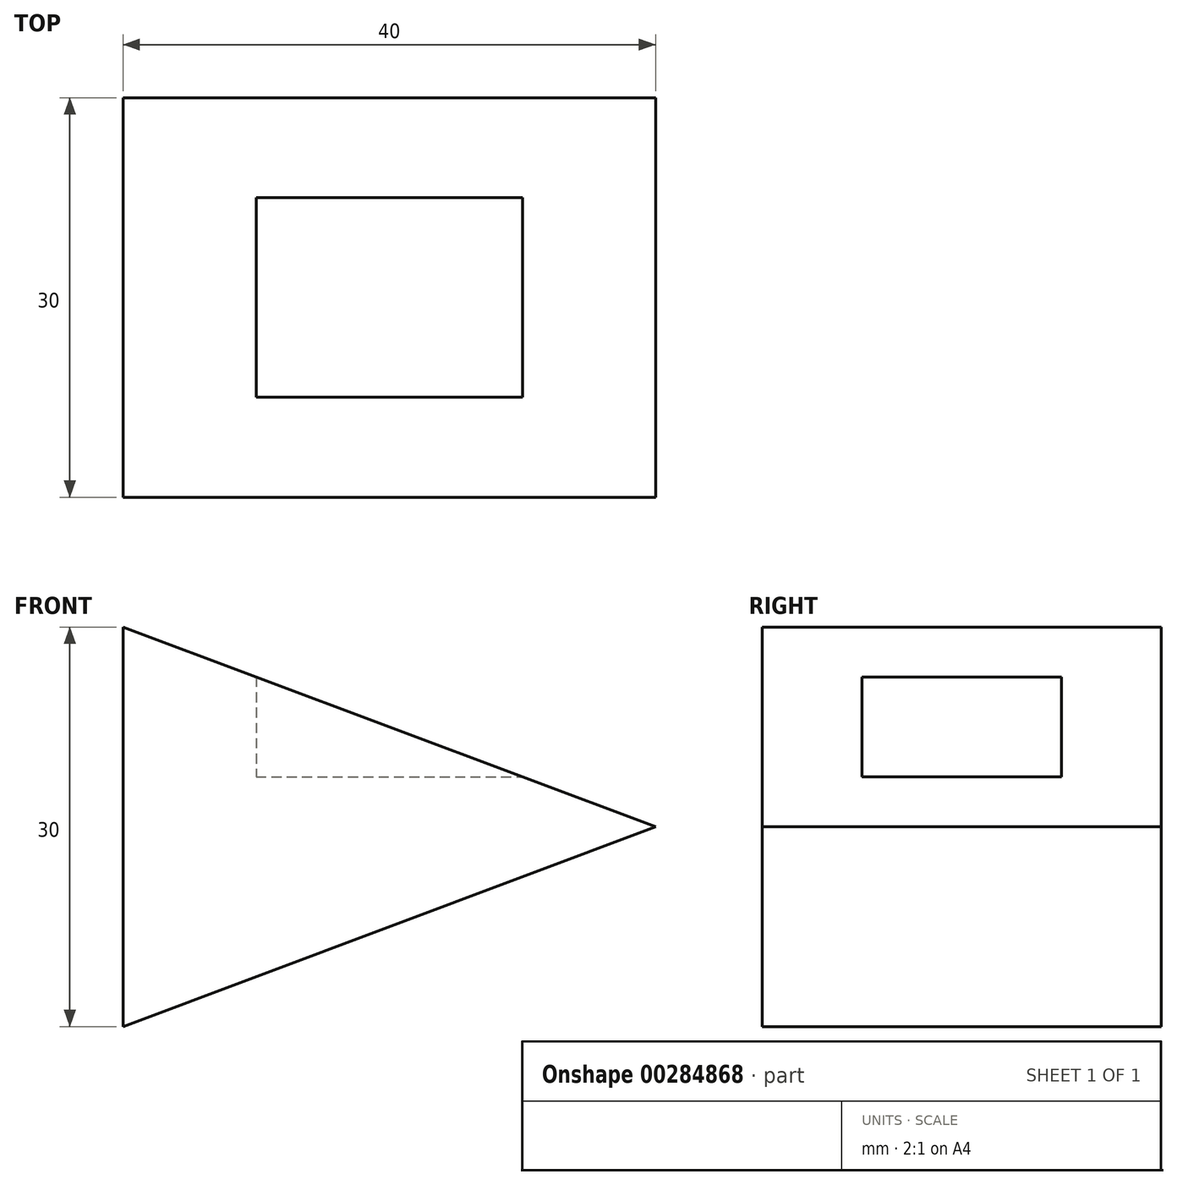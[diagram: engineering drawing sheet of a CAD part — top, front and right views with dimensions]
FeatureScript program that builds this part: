
annotation { "Feature Type Name" : "Feature", "Feature Type Description" : "" }
export const myFeature = defineFeature(function(context is Context, id is Id, definition is map)
    precondition{}
    {
        {
            var Q0;
            Q0=qCreatedBy(makeId("Front.planeOp"),FACE);
            var sketch = newSketch(context, id + "F0", { "sketchPlane" : qUnion([Q0])});
            skLineSegment(sketch, "E0.bottom", {"start": v(0, 0) * mm, "end": v(40, 0) * mm});
            skLineSegment(sketch, "E0.top", {"start": v(0, 30) * mm, "end": v(40, 30) * mm});
            skLineSegment(sketch, "E0.left", {"start": v(0, 0) * mm, "end": v(0, 30) * mm});
            skLineSegment(sketch, "E0.right", {"start": v(40, 0) * mm, "end": v(40, 30) * mm});
            skLineSegment(sketch, "E1", {"start": v(0, 30) * mm, "end": v(40, 15) * mm});
            skLineSegment(sketch, "E2.bottom", {"start": v(10, 26.25) * mm, "end": v(30, 26.25) * mm});
            skLineSegment(sketch, "E2.top", {"start": v(10, 18.75) * mm, "end": v(30, 18.75) * mm});
            skLineSegment(sketch, "E2.left", {"start": v(10, 26.25) * mm, "end": v(10, 18.75) * mm});
            skLineSegment(sketch, "E2.right", {"start": v(30, 26.25) * mm, "end": v(30, 18.75) * mm});
            skLineSegment(sketch, "E3", {"start": v(40, 15) * mm, "end": v(0, 0) * mm});
            skSolve(sketch);
        }
        {
            var Q0;
            {var subQ4=sQuery(id+"F0.wireOp",EDGE,"E0.bottom");Q0=makeQuery(id+"F0.imprint","IMPRINT",FACE,{"disambiguationData":[TD([[makeQuery(id+"F0.imprint","IMPRINT",EDGE,{"derivedFrom":subQ4}),1.0]])]});}
            var Q1;
            {var subQ2=sQuery(id+"F0.wireOp",EDGE,"E2.top");Q1=makeQuery(id+"F0.imprint","IMPRINT",FACE,{"disambiguationData":[TD([[makeQuery(id+"F0.imprint","IMPRINT",EDGE,{"derivedFrom":subQ2}),1.0]])]});}
            var Q2;
            {var subQ2=sQuery(id+"F0.wireOp",EDGE,"E0.left");Q2=makeQuery(id+"F0.imprint","IMPRINT",FACE,{"disambiguationData":[TD([[makeQuery(id+"F0.imprint","IMPRINT",EDGE,{"derivedFrom":subQ2}),-1.0]])]});}
            extrude(context, id + "F1", {"entities" : qUnion([Q0, Q1, Q2]), "depth" : 30 * mm, "symmetric" : true});
        }
        {
            var Q0;
            {var subQ2=sQuery(id+"F0.wireOp",EDGE,"E2.top");Q0=makeQuery(id+"F0.imprint","IMPRINT",FACE,{"disambiguationData":[TD([[makeQuery(id+"F0.imprint","IMPRINT",EDGE,{"derivedFrom":subQ2}),1.0]])]});}
            extrude(context, id + "F2", {"entities" : qUnion([Q0]), "operationType" : NewBodyOperationType.REMOVE, "oppositeDirection" : true, "depth" : 15 * mm, "symmetric" : true});
        }
        {
            var Q0;
            {var subQ0=sQuery(id+"F0.wireOp",EDGE,"E0.bottom");Q0=makeQuery(id+"F0.imprint","IMPRINT",FACE,{"disambiguationData":[TD([[makeQuery(id+"F0.imprint","IMPRINT",EDGE,{"derivedFrom":subQ0}),1.0]])]});}
            extrude(context, id + "F3", {"entities" : qUnion([Q0]), "operationType" : NewBodyOperationType.REMOVE, "oppositeDirection" : true, "depth" : 30 * mm, "symmetric" : true});
        }
    });
